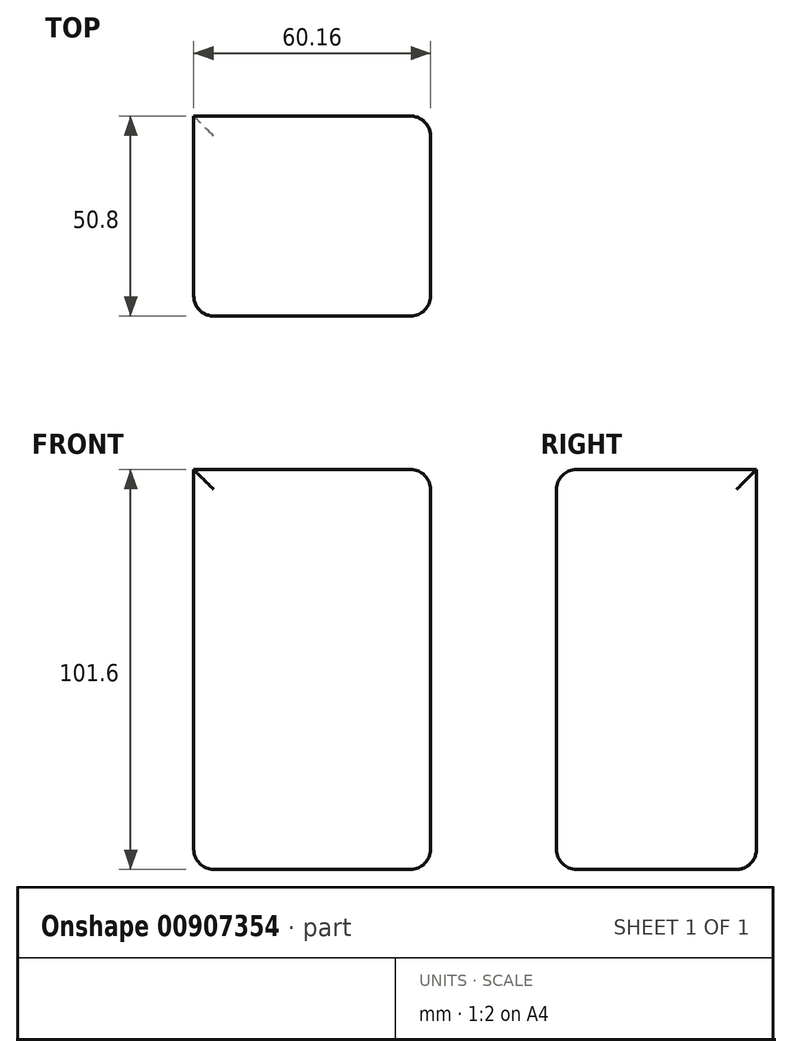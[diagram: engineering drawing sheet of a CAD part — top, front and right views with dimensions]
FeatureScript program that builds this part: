
annotation { "Feature Type Name" : "Feature", "Feature Type Description" : "" }
export const myFeature = defineFeature(function(context is Context, id is Id, definition is map)
    precondition{}
    {
        {
            var Q0;
            Q0=qCreatedBy(makeId("Front.planeOp"),FACE);
            var sketch = newSketch(context, id + "F0", { "sketchPlane" : qUnion([Q0])});
            skLineSegment(sketch, "E0.bottom", {"start": v(0, -20.4) * mm, "end": v(-60.16, -20.4) * mm});
            skLineSegment(sketch, "E0.top", {"start": v(0, 81.2) * mm, "end": v(-60.16, 81.2) * mm});
            skLineSegment(sketch, "E0.left", {"start": v(0, -20.4) * mm, "end": v(0, 81.2) * mm});
            skLineSegment(sketch, "E0.right", {"start": v(-60.16, -20.4) * mm, "end": v(-60.16, 81.2) * mm});
            skPoint(sketch, "E0.middle", {"position": v(-30.08, 30.4) * mm});
            skLineSegment(sketch, "E1.bottom", {"start": v(-60.16, 30.4) * mm, "end": v(-60.16, 30.4) * mm});
            skLineSegment(sketch, "E1.top", {"start": v(-60.16, 30.4) * mm, "end": v(-60.16, 30.4) * mm});
            skLineSegment(sketch, "E1.left", {"start": v(-60.16, 30.4) * mm, "end": v(-60.16, 30.4) * mm});
            skLineSegment(sketch, "E1.right", {"start": v(-60.16, 30.4) * mm, "end": v(-60.16, 30.4) * mm});
            skPoint(sketch, "E1.middle", {"position": v(-60.16, 30.4) * mm});
            skSolve(sketch);
        }
        {
            var Q0;
            Q0 = qSketchRegion(id + "F0", true);
            extrude(context, id + "F1", {"entities" : qUnion([Q0]), "depth" : 50.8 * mm, "offsetDistance" : 25.4 * mm});
        }
        {
            var Q0;
            Q0=makeQuery(id+"F1.opExtrude","CAP_EDGE",EDGE,{"disambiguationData":[OSD([sQuery(id+"F0.wireOp",EDGE,"E0.top")])],"isStart":false});
            var Q1;
            Q1=makeQuery(id+"F1.opExtrude","CAP_EDGE",EDGE,{"disambiguationData":[OSD([sQuery(id+"F0.wireOp",EDGE,"E0.right")])],"isStart":false});
            var Q2;
            Q2=makeQuery(id+"F1.opExtrude","SWEPT_FACE",FACE,{"disambiguationData":[OSD([sQuery(id+"F0.wireOp",EDGE,"E0.bottom")])]});
            var Q3;
            Q3=makeQuery(id+"F1.opExtrude","SWEPT_FACE",FACE,{"disambiguationData":[OSD([sQuery(id+"F0.wireOp",EDGE,"E0.left")])]});
            fillet(context, id + "F2", {"entities" : qUnion([Q0, Q1, Q2, Q3]), "radius" : 5.08 * mm, "tangentPropagation" : true, "allowEdgeOverflow" : false});
        }
    });
